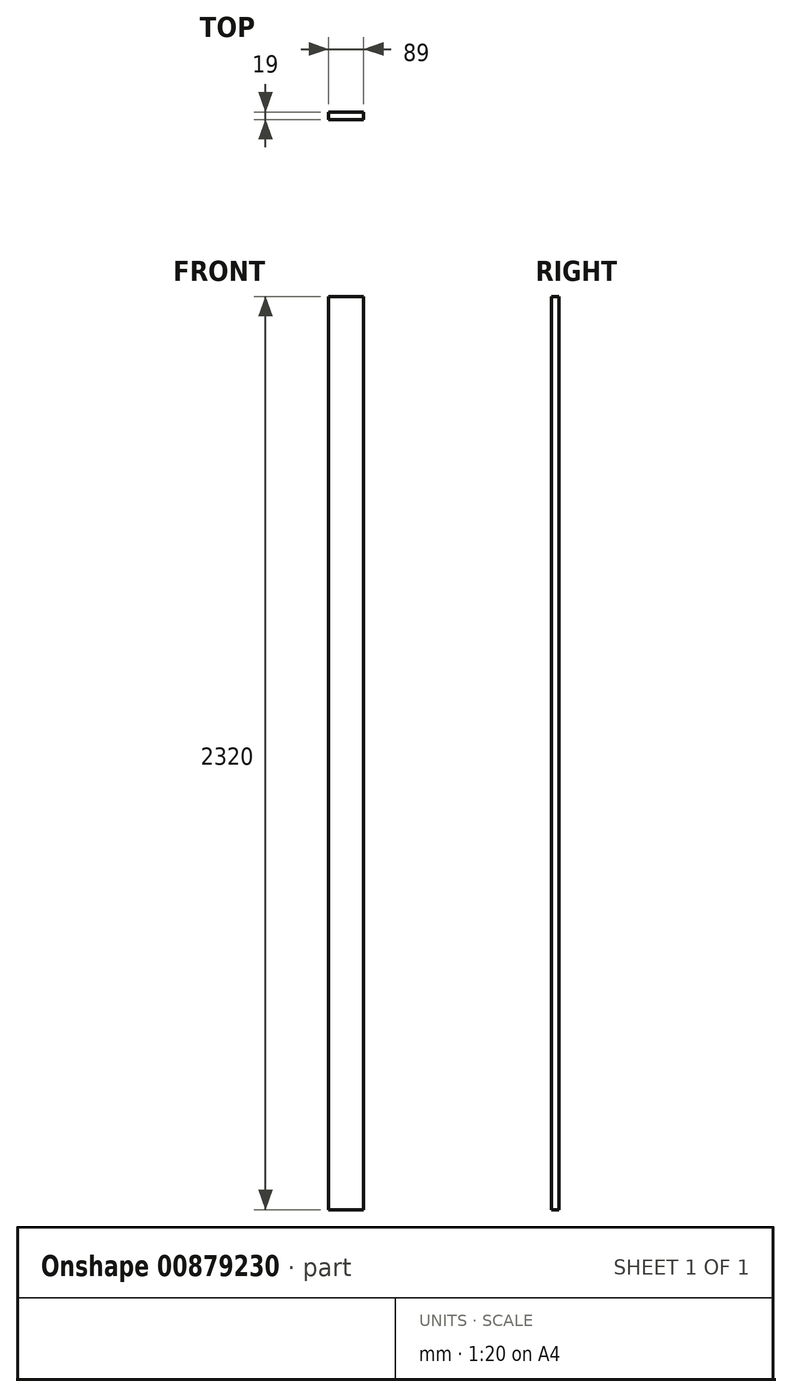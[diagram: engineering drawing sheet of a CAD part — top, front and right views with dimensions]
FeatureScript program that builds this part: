
annotation { "Feature Type Name" : "Feature", "Feature Type Description" : "" }
export const myFeature = defineFeature(function(context is Context, id is Id, definition is map)
    precondition{}
    {
        {
            var Q0;
            Q0=qCreatedBy(makeId("Front.planeOp"),FACE);
            var sketch = newSketch(context, id + "F0", { "sketchPlane" : qUnion([Q0])});
            skLineSegment(sketch, "E0.bottom", {"start": v(-44.5, 1160) * mm, "end": v(44.5, 1160) * mm});
            skLineSegment(sketch, "E0.top", {"start": v(-44.5, -1160) * mm, "end": v(44.5, -1160) * mm});
            skLineSegment(sketch, "E0.left", {"start": v(-44.5, 1160) * mm, "end": v(-44.5, -1160) * mm});
            skLineSegment(sketch, "E0.right", {"start": v(44.5, 1160) * mm, "end": v(44.5, -1160) * mm});
            skSolve(sketch);
        }
        {
            var Q0;
            Q0 = qSketchRegion(id + "F0", true);
            extrude(context, id + "F1", {"entities" : qUnion([Q0]), "depth" : 19 * mm, "offsetDistance" : 25 * mm, "symmetric" : true});
        }
    });
